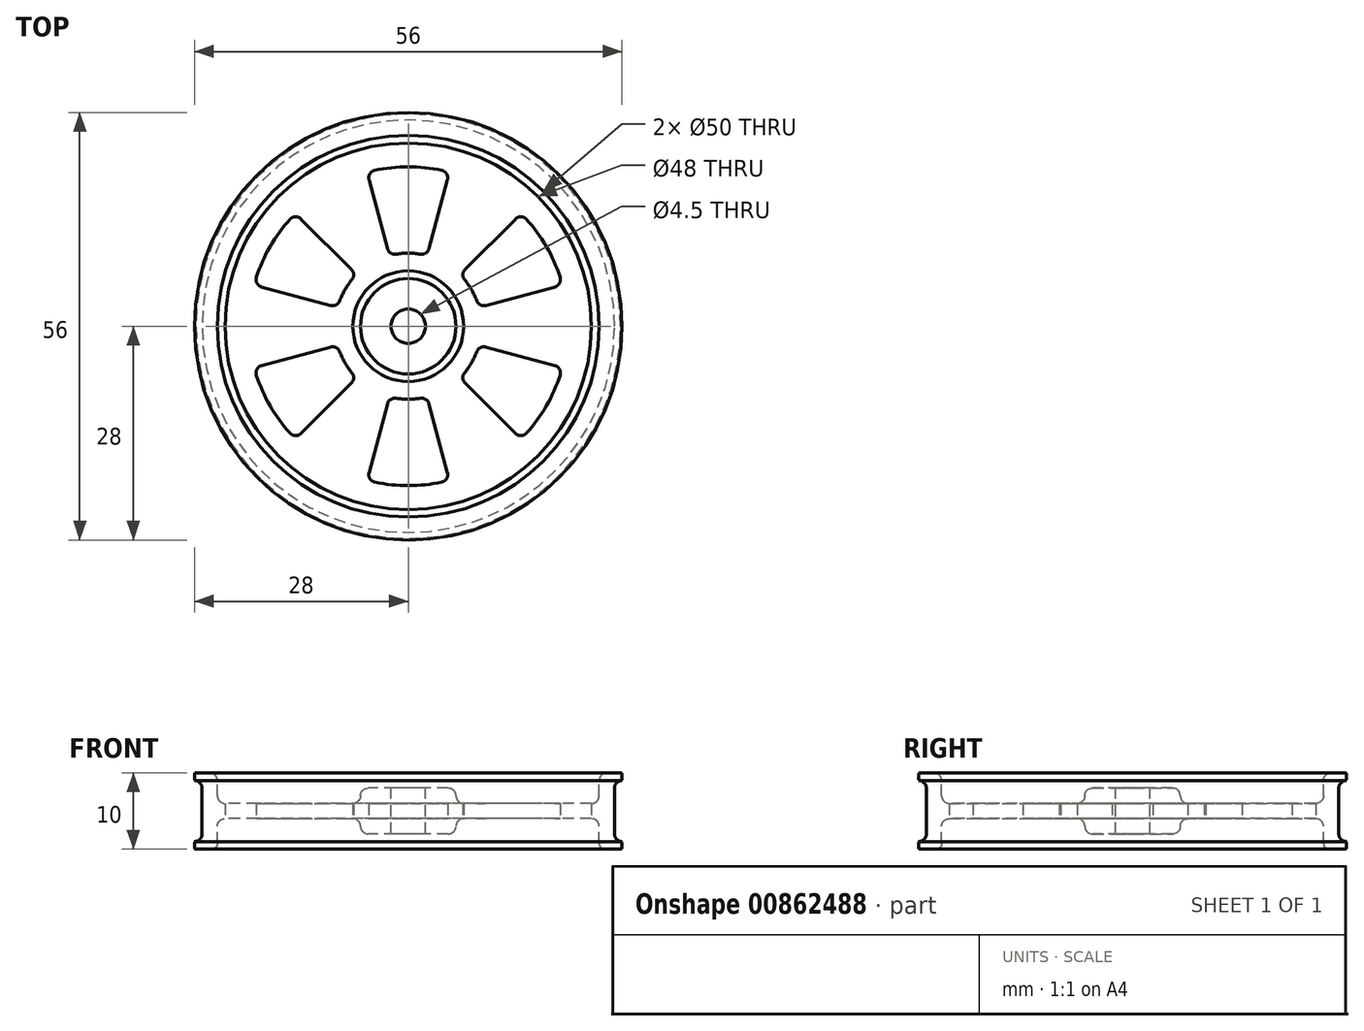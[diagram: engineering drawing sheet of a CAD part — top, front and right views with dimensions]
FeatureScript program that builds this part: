
annotation { "Feature Type Name" : "Feature", "Feature Type Description" : "" }
export const myFeature = defineFeature(function(context is Context, id is Id, definition is map)
    precondition{}
    {
        {
            var Q0;
            Q0=qCreatedBy(makeId("Front.planeOp"),FACE);
            var sketch = newSketch(context, id + "F0", { "sketchPlane" : qUnion([Q0])});
            skLineSegment(sketch, "E0.bottom", {"start": v(7.25, 1) * mm, "end": v(24, 1) * mm});
            skLineSegment(sketch, "E0.left", {"start": v(0, 1) * mm, "end": v(0, -1) * mm});
            skLineSegment(sketch, "E1", {"start": v(25, 2) * mm, "end": v(25, 4) * mm});
            skLineSegment(sketch, "E2", {"start": v(26, 5) * mm, "end": v(27.8, 5) * mm});
            skLineSegment(sketch, "E3", {"start": v(28, 4.8) * mm, "end": v(28, 4.2) * mm});
            skLineSegment(sketch, "E4", {"start": v(28, 4) * mm, "end": v(27.8, 4) * mm});
            skLineSegment(sketch, "E5", {"start": v(27, 3) * mm, "end": v(27, 0) * mm});
            skLineSegment(sketch, "E6.MirrorCS", {"start": v(25, -1) * mm, "end": v(25, -3) * mm});
            skLineSegment(sketch, "E7.MirrorCS", {"start": v(27, -2) * mm, "end": v(27, 2) * mm});
            skLineSegment(sketch, "E8.MirrorCS", {"start": v(7.25, -1) * mm, "end": v(24, -1) * mm});
            skLineSegment(sketch, "E9.MirrorCS", {"start": v(25, -2) * mm, "end": v(25, -4.27) * mm});
            skLineSegment(sketch, "E10.MirrorCS", {"start": v(25.73, -5) * mm, "end": v(27.8, -5) * mm});
            skLineSegment(sketch, "E11.MirrorCS", {"start": v(28, -4.8) * mm, "end": v(28, -4.2) * mm});
            skLineSegment(sketch, "E12.MirrorCS", {"start": v(28, -4) * mm, "end": v(27.8, -4) * mm});
            skLineSegment(sketch, "E13.MirrorCS", {"start": v(27, -3) * mm, "end": v(27, 0) * mm});
            skPoint(sketch, "E14.orphan", {"position": v(25, 1) * mm});
            skArc(sketch, "E15.filletArc", {"start": v(24, 1) * mm, "mid": v(24.7, 1.3) * mm, "end": v(25, 2) * mm});
            skPoint(sketch, "E16.visualSharp", {"position": v(25, 5) * mm});
            skArc(sketch, "E16.filletArc", {"start": v(26, 5) * mm, "mid": v(25.3, 4.7) * mm, "end": v(25, 4) * mm});
            skPoint(sketch, "E17.visualSharp", {"position": v(27, 4) * mm});
            skArc(sketch, "E17.filletArc", {"start": v(28, 4) * mm, "mid": v(27.3, 3.7) * mm, "end": v(27, 3) * mm});
            skPoint(sketch, "E18.visualSharp", {"position": v(27, -4) * mm});
            skArc(sketch, "E18.filletArc", {"start": v(27, -3) * mm, "mid": v(27.3, -3.7) * mm, "end": v(28, -4) * mm});
            skPoint(sketch, "E19.visualSharp", {"position": v(25, -5) * mm});
            skArc(sketch, "E19.filletArc", {"start": v(25, -4.27) * mm, "mid": v(25.21, -4.79) * mm, "end": v(25.73, -5) * mm});
            skPoint(sketch, "E20.visualSharp", {"position": v(25, -1) * mm});
            skArc(sketch, "E20.filletArc", {"start": v(25, -2) * mm, "mid": v(24.7, -1.3) * mm, "end": v(24, -1) * mm});
            skPoint(sketch, "E21.visualSharp", {"position": v(28, 5) * mm});
            skArc(sketch, "E21.filletArc", {"start": v(28, 4.8) * mm, "mid": v(27.94, 4.94) * mm, "end": v(27.8, 5) * mm});
            skPoint(sketch, "E22.visualSharp", {"position": v(28, -5) * mm});
            skArc(sketch, "E22.filletArc", {"start": v(27.8, -5) * mm, "mid": v(27.94, -4.94) * mm, "end": v(28, -4.8) * mm});
            skPoint(sketch, "E23.visualSharp", {"position": v(28, 4) * mm});
            skArc(sketch, "E23.filletArc", {"start": v(27.8, 4) * mm, "mid": v(27.94, 4.06) * mm, "end": v(28, 4.2) * mm});
            skPoint(sketch, "E24.visualSharp", {"position": v(28, -4) * mm});
            skArc(sketch, "E24.filletArc", {"start": v(28, -4.2) * mm, "mid": v(27.94, -4.06) * mm, "end": v(27.8, -4) * mm});
            skLineSegment(sketch, "E25", {"start": v(0, 6.54) * mm, "end": v(0, 1) * mm, "construction": true});
            skLineSegment(sketch, "E26", {"start": v(2.25, -2.5) * mm, "end": v(2.25, 1) * mm});
            skPoint(sketch, "E27.orphan", {"position": v(0, -1) * mm});
            skLineSegment(sketch, "E28.trimOffspring", {"start": v(0, -1) * mm, "end": v(0, -8.8) * mm, "construction": true});
            skLineSegment(sketch, "E29.top", {"start": v(2.25, -3) * mm, "end": v(5.25, -3) * mm});
            skLineSegment(sketch, "E29.left", {"start": v(2.25, -1) * mm, "end": v(2.25, -3) * mm});
            skLineSegment(sketch, "E29.right", {"start": v(6.25, -2) * mm, "end": v(6.25, -2) * mm});
            skPoint(sketch, "E30.visualSharp", {"position": v(6.25, -3) * mm});
            skArc(sketch, "E30.filletArc", {"start": v(5.25, -3) * mm, "mid": v(5.96, -2.7) * mm, "end": v(6.25, -2) * mm});
            skPoint(sketch, "E31.newPointA", {"position": v(6.25, -1) * mm});
            skArc(sketch, "E31.filletArc", {"start": v(7.25, -1) * mm, "mid": v(6.54, -1.3) * mm, "end": v(6.25, -2) * mm});
            skLineSegment(sketch, "E32.MirrorCS", {"start": v(2.25, 1) * mm, "end": v(2.25, 3) * mm});
            skLineSegment(sketch, "E33.MirrorCS", {"start": v(2.25, 3) * mm, "end": v(5.25, 3) * mm});
            skArc(sketch, "E34.MirrorCS", {"start": v(5.25, 3) * mm, "mid": v(5.96, 2.7) * mm, "end": v(6.25, 2) * mm});
            skArc(sketch, "E35.MirrorCS", {"start": v(7.25, 1) * mm, "mid": v(6.54, 1.3) * mm, "end": v(6.25, 2) * mm});
            skSolve(sketch);
        }
        {
            var Q0;
            Q0=makeQuery(id+"F0.imprint","IMPRINT",FACE,{"disambiguationData":[TD([[makeQuery(id+"F0.imprint","IMPRINT",EDGE,{"derivedFrom":sQuery(id+"F0.wireOp",EDGE,"E0.bottom")}),-1.0]])]});
            var Q1;
            Q1=sQuery(id+"F0.wireOp",EDGE,"E25");
            revolve(context, id + "F1", {"surfaceOperationType" : NewSurfaceOperationType.NEW, "entities" : qUnion([Q0]), "axis" : qUnion([Q1]), "revolveType" : RevolveType.FULL});
        }
        {
            var Q0;
            Q0=makeQuery(id+"F1.opRevolve","SWEPT_FACE",FACE,{"disambiguationData":[OSD([sQuery(id+"F0.wireOp",EDGE,"E8.MirrorCS")])]});
            var sketch = newSketch(context, id + "F2", { "sketchPlane" : qUnion([Q0])});
            skCircle(sketch, "E36", {"center": v(0, 0) * mm, "radius": 2.75 * mm});
            skSolve(sketch);
        }
        {
            var Q0;
            {var subQ0=sQuery(id+"F0.wireOp",EDGE,"E8.MirrorCS");Q0=makeQuery(id+"F2.imprint","IMPRINT",FACE,{"disambiguationData":[TD([[makeQuery(id+"F2.imprint","IMPRINT",EDGE,{"derivedFrom":makeQuery(id+"F1.opRevolve","SWEPT_EDGE",EDGE,{"disambiguationData":[OSD([subQ0,sQuery(id+"F0.wireOp",EDGE,"E31.filletArc")])]})}),1.0]])]});}
            var sketch = newSketch(context, id + "F3", { "sketchPlane" : qUnion([Q0])});
            skLineSegment(sketch, "E37", {"start": v(-2.72, 10.16) * mm, "end": v(-5.14, 19.18) * mm, "construction": true});
            skLineSegment(sketch, "E38", {"start": v(-5.14, 19.18) * mm, "end": v(-2.72, 10.16) * mm, "construction": true});
            skLineSegment(sketch, "E39", {"start": v(2.72, 10.16) * mm, "end": v(5.14, 19.18) * mm, "construction": true});
            skArc(sketch, "E40", {"start": v(-4.38, 20.42) * mm, "mid": v(0, 20.88) * mm, "end": v(4.38, 20.42) * mm});
            skArc(sketch, "E41", {"start": v(-1.6, 9.44) * mm, "mid": v(0, 9.57) * mm, "end": v(1.6, 9.44) * mm});
            skLineSegment(sketch, "E42", {"start": v(-5.14, 19.18) * mm, "end": v(-2.72, 10.16) * mm});
            skLineSegment(sketch, "E43", {"start": v(5.14, 19.18) * mm, "end": v(2.72, 10.16) * mm});
            skArc(sketch, "E44.filletArc", {"start": v(-4.38, 20.42) * mm, "mid": v(-5.03, 19.96) * mm, "end": v(-5.14, 19.18) * mm});
            skArc(sketch, "E45.filletArc", {"start": v(5.14, 19.18) * mm, "mid": v(5.03, 19.96) * mm, "end": v(4.38, 20.42) * mm});
            skArc(sketch, "E46.filletArc", {"start": v(-2.72, 10.16) * mm, "mid": v(-2.3, 9.58) * mm, "end": v(-1.6, 9.44) * mm});
            skArc(sketch, "E47.filletArc", {"start": v(1.6, 9.44) * mm, "mid": v(2.3, 9.58) * mm, "end": v(2.72, 10.16) * mm});
            skLineSegment(sketch, "E48.trimOffspring", {"start": v(-5.4, 20.17) * mm, "end": v(-8.77, 32.74) * mm, "construction": true});
            skLineSegment(sketch, "E49.trimOffspring", {"start": v(-2.48, 9.24) * mm, "end": v(0, 0) * mm, "construction": true});
            skLineSegment(sketch, "E50.1.0", {"start": v(-7.44, 7.44) * mm, "end": v(-14.04, 14.04) * mm, "construction": true});
            skArc(sketch, "E50.1.1", {"start": v(-8.97, 3.34) * mm, "mid": v(-8.29, 4.79) * mm, "end": v(-7.38, 6.1) * mm});
            skArc(sketch, "E50.1.2", {"start": v(-19.87, 6.41) * mm, "mid": v(-18.09, 10.44) * mm, "end": v(-15.5, 14) * mm});
            skLineSegment(sketch, "E50.1.3", {"start": v(-19.18, 5.14) * mm, "end": v(-10.16, 2.72) * mm, "construction": true});
            skLineSegment(sketch, "E50.1.4", {"start": v(-10.16, 2.72) * mm, "end": v(-19.18, 5.14) * mm, "construction": true});
            skLineSegment(sketch, "E50.1.5", {"start": v(-14.04, 14.04) * mm, "end": v(-7.44, 7.44) * mm});
            skArc(sketch, "E50.1.6", {"start": v(-10.16, 2.72) * mm, "mid": v(-9.45, 2.8) * mm, "end": v(-8.97, 3.34) * mm});
            skArc(sketch, "E50.1.7", {"start": v(-7.38, 6.1) * mm, "mid": v(-7.15, 6.78) * mm, "end": v(-7.44, 7.44) * mm});
            skLineSegment(sketch, "E50.1.8", {"start": v(-19.18, 5.14) * mm, "end": v(-10.16, 2.72) * mm});
            skArc(sketch, "E50.1.9", {"start": v(-14.04, 14.04) * mm, "mid": v(-14.77, 14.33) * mm, "end": v(-15.5, 14) * mm});
            skArc(sketch, "E50.1.10", {"start": v(-19.87, 6.41) * mm, "mid": v(-19.8, 5.63) * mm, "end": v(-19.18, 5.14) * mm});
            skLineSegment(sketch, "E50.2.0", {"start": v(-10.16, -2.72) * mm, "end": v(-19.18, -5.14) * mm, "construction": true});
            skArc(sketch, "E50.2.1", {"start": v(-7.38, -6.1) * mm, "mid": v(-8.29, -4.79) * mm, "end": v(-8.97, -3.34) * mm});
            skArc(sketch, "E50.2.2", {"start": v(-15.5, -14) * mm, "mid": v(-18.09, -10.44) * mm, "end": v(-19.87, -6.41) * mm});
            skLineSegment(sketch, "E50.2.3", {"start": v(-14.04, -14.04) * mm, "end": v(-7.44, -7.44) * mm, "construction": true});
            skLineSegment(sketch, "E50.2.4", {"start": v(-7.44, -7.44) * mm, "end": v(-14.04, -14.04) * mm, "construction": true});
            skLineSegment(sketch, "E50.2.5", {"start": v(-19.18, -5.14) * mm, "end": v(-10.16, -2.72) * mm});
            skArc(sketch, "E50.2.6", {"start": v(-7.44, -7.44) * mm, "mid": v(-7.15, -6.78) * mm, "end": v(-7.38, -6.1) * mm});
            skArc(sketch, "E50.2.7", {"start": v(-8.97, -3.34) * mm, "mid": v(-9.45, -2.8) * mm, "end": v(-10.16, -2.72) * mm});
            skLineSegment(sketch, "E50.2.8", {"start": v(-14.04, -14.04) * mm, "end": v(-7.44, -7.44) * mm});
            skArc(sketch, "E50.2.9", {"start": v(-19.18, -5.14) * mm, "mid": v(-19.8, -5.63) * mm, "end": v(-19.87, -6.41) * mm});
            skArc(sketch, "E50.2.10", {"start": v(-15.5, -14) * mm, "mid": v(-14.77, -14.33) * mm, "end": v(-14.04, -14.04) * mm});
            skLineSegment(sketch, "E50.3.0", {"start": v(-2.72, -10.16) * mm, "end": v(-5.14, -19.18) * mm, "construction": true});
            skArc(sketch, "E50.3.1", {"start": v(1.6, -9.44) * mm, "mid": v(0, -9.57) * mm, "end": v(-1.6, -9.44) * mm});
            skArc(sketch, "E50.3.2", {"start": v(4.38, -20.42) * mm, "mid": v(0, -20.88) * mm, "end": v(-4.38, -20.42) * mm});
            skLineSegment(sketch, "E50.3.3", {"start": v(5.14, -19.18) * mm, "end": v(2.72, -10.16) * mm, "construction": true});
            skLineSegment(sketch, "E50.3.4", {"start": v(2.72, -10.16) * mm, "end": v(5.14, -19.18) * mm, "construction": true});
            skLineSegment(sketch, "E50.3.5", {"start": v(-5.14, -19.18) * mm, "end": v(-2.72, -10.16) * mm});
            skArc(sketch, "E50.3.6", {"start": v(2.72, -10.16) * mm, "mid": v(2.3, -9.58) * mm, "end": v(1.6, -9.44) * mm});
            skArc(sketch, "E50.3.7", {"start": v(-1.6, -9.44) * mm, "mid": v(-2.3, -9.58) * mm, "end": v(-2.72, -10.16) * mm});
            skLineSegment(sketch, "E50.3.8", {"start": v(5.14, -19.18) * mm, "end": v(2.72, -10.16) * mm});
            skArc(sketch, "E50.3.9", {"start": v(-5.14, -19.18) * mm, "mid": v(-5.03, -19.96) * mm, "end": v(-4.38, -20.42) * mm});
            skArc(sketch, "E50.3.10", {"start": v(4.38, -20.42) * mm, "mid": v(5.03, -19.96) * mm, "end": v(5.14, -19.18) * mm});
            skLineSegment(sketch, "E50.4.0", {"start": v(7.44, -7.44) * mm, "end": v(14.04, -14.04) * mm, "construction": true});
            skArc(sketch, "E50.4.1", {"start": v(8.97, -3.34) * mm, "mid": v(8.29, -4.79) * mm, "end": v(7.38, -6.1) * mm});
            skArc(sketch, "E50.4.2", {"start": v(19.87, -6.41) * mm, "mid": v(18.09, -10.44) * mm, "end": v(15.5, -14) * mm});
            skLineSegment(sketch, "E50.4.3", {"start": v(19.18, -5.14) * mm, "end": v(10.16, -2.72) * mm, "construction": true});
            skLineSegment(sketch, "E50.4.4", {"start": v(10.16, -2.72) * mm, "end": v(19.18, -5.14) * mm, "construction": true});
            skLineSegment(sketch, "E50.4.5", {"start": v(14.04, -14.04) * mm, "end": v(7.44, -7.44) * mm});
            skArc(sketch, "E50.4.6", {"start": v(10.16, -2.72) * mm, "mid": v(9.45, -2.8) * mm, "end": v(8.97, -3.34) * mm});
            skArc(sketch, "E50.4.7", {"start": v(7.38, -6.1) * mm, "mid": v(7.15, -6.78) * mm, "end": v(7.44, -7.44) * mm});
            skLineSegment(sketch, "E50.4.8", {"start": v(19.18, -5.14) * mm, "end": v(10.16, -2.72) * mm});
            skArc(sketch, "E50.4.9", {"start": v(14.04, -14.04) * mm, "mid": v(14.77, -14.33) * mm, "end": v(15.5, -14) * mm});
            skArc(sketch, "E50.4.10", {"start": v(19.87, -6.41) * mm, "mid": v(19.8, -5.63) * mm, "end": v(19.18, -5.14) * mm});
            skLineSegment(sketch, "E50.5.0", {"start": v(10.16, 2.72) * mm, "end": v(19.18, 5.14) * mm, "construction": true});
            skArc(sketch, "E50.5.1", {"start": v(7.38, 6.1) * mm, "mid": v(8.29, 4.79) * mm, "end": v(8.97, 3.34) * mm});
            skArc(sketch, "E50.5.2", {"start": v(15.5, 14) * mm, "mid": v(18.09, 10.44) * mm, "end": v(19.87, 6.41) * mm});
            skLineSegment(sketch, "E50.5.3", {"start": v(14.04, 14.04) * mm, "end": v(7.44, 7.44) * mm, "construction": true});
            skLineSegment(sketch, "E50.5.4", {"start": v(7.44, 7.44) * mm, "end": v(14.04, 14.04) * mm, "construction": true});
            skLineSegment(sketch, "E50.5.5", {"start": v(19.18, 5.14) * mm, "end": v(10.16, 2.72) * mm});
            skArc(sketch, "E50.5.6", {"start": v(7.44, 7.44) * mm, "mid": v(7.15, 6.78) * mm, "end": v(7.38, 6.1) * mm});
            skArc(sketch, "E50.5.7", {"start": v(8.97, 3.34) * mm, "mid": v(9.45, 2.8) * mm, "end": v(10.16, 2.72) * mm});
            skLineSegment(sketch, "E50.5.8", {"start": v(14.04, 14.04) * mm, "end": v(7.44, 7.44) * mm});
            skArc(sketch, "E50.5.9", {"start": v(19.18, 5.14) * mm, "mid": v(19.8, 5.63) * mm, "end": v(19.87, 6.41) * mm});
            skArc(sketch, "E50.5.10", {"start": v(15.5, 14) * mm, "mid": v(14.77, 14.33) * mm, "end": v(14.04, 14.04) * mm});
            skSolve(sketch);
        }
        {
            var Q0;
            Q0=makeQuery(id+"F3.imprint","IMPRINT",FACE,{"disambiguationData":[TD([[makeQuery(id+"F3.imprint","IMPRINT",EDGE,{"derivedFrom":sQuery(id+"F3.wireOp",EDGE,"E40")}),-1.0]])]});
            var Q1;
            Q1=makeQuery(id+"F3.imprint","IMPRINT",FACE,{"disambiguationData":[TD([[makeQuery(id+"F3.imprint","IMPRINT",EDGE,{"derivedFrom":sQuery(id+"F3.wireOp",EDGE,"E50.5.1")}),1.0]])]});
            var Q2;
            Q2=makeQuery(id+"F3.imprint","IMPRINT",FACE,{"disambiguationData":[TD([[makeQuery(id+"F3.imprint","IMPRINT",EDGE,{"derivedFrom":sQuery(id+"F3.wireOp",EDGE,"E50.4.1")}),1.0]])]});
            var Q3;
            Q3=makeQuery(id+"F3.imprint","IMPRINT",FACE,{"disambiguationData":[TD([[makeQuery(id+"F3.imprint","IMPRINT",EDGE,{"derivedFrom":sQuery(id+"F3.wireOp",EDGE,"E50.3.1")}),1.0]])]});
            var Q4;
            Q4=makeQuery(id+"F3.imprint","IMPRINT",FACE,{"disambiguationData":[TD([[makeQuery(id+"F3.imprint","IMPRINT",EDGE,{"derivedFrom":sQuery(id+"F3.wireOp",EDGE,"E50.2.1")}),1.0]])]});
            var Q5;
            Q5=makeQuery(id+"F3.imprint","IMPRINT",FACE,{"disambiguationData":[TD([[makeQuery(id+"F3.imprint","IMPRINT",EDGE,{"derivedFrom":sQuery(id+"F3.wireOp",EDGE,"E50.1.1")}),1.0]])]});
            extrude(context, id + "F4", {"entities" : qUnion([Q0, Q1, Q2, Q3, Q4, Q5]), "operationType" : NewBodyOperationType.REMOVE, "oppositeDirection" : true, "depth" : 2 * mm, "offsetDistance" : 25 * mm});
        }
    });
